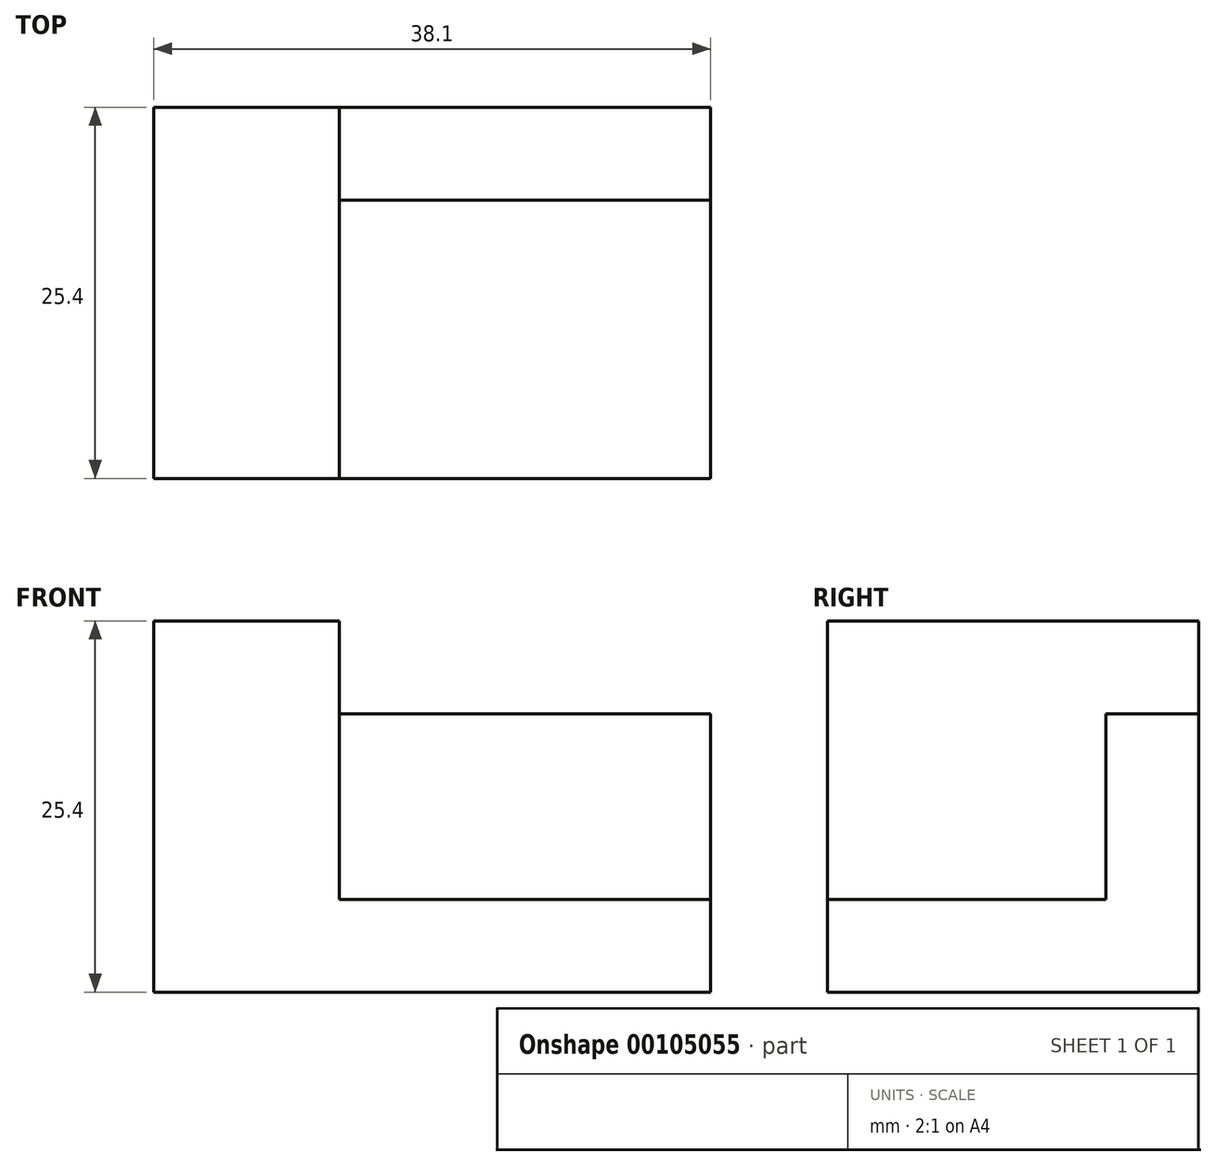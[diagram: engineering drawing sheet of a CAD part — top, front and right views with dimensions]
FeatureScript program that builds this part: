
annotation { "Feature Type Name" : "Feature", "Feature Type Description" : "" }
export const myFeature = defineFeature(function(context is Context, id is Id, definition is map)
    precondition{}
    {
        {
            var Q0;
            Q0=qCreatedBy(makeId("Right.planeOp"),FACE);
            var sketch = newSketch(context, id + "F0", { "sketchPlane" : qUnion([Q0])});
            skLineSegment(sketch, "E0.bottom", {"start": v(0, 0) * mm, "end": v(25.4, 0) * mm});
            skLineSegment(sketch, "E0.top", {"start": v(0, -25.4) * mm, "end": v(25.4, -25.4) * mm});
            skLineSegment(sketch, "E0.left", {"start": v(0, 0) * mm, "end": v(0, -25.4) * mm});
            skLineSegment(sketch, "E0.right", {"start": v(25.4, 0) * mm, "end": v(25.4, -25.4) * mm});
            skLineSegment(sketch, "E1.bottom", {"start": v(25.4, -6.35) * mm, "end": v(19.05, -6.35) * mm});
            skLineSegment(sketch, "E1.top", {"start": v(25.4, -25.4) * mm, "end": v(19.05, -25.4) * mm});
            skLineSegment(sketch, "E1.left", {"start": v(25.4, -6.35) * mm, "end": v(25.4, -25.4) * mm});
            skLineSegment(sketch, "E1.right", {"start": v(19.05, -6.35) * mm, "end": v(19.05, -19.05) * mm});
            skLineSegment(sketch, "E2.bottom", {"start": v(19.05, -19.05) * mm, "end": v(0, -19.05) * mm});
            skLineSegment(sketch, "E2.top", {"start": v(19.05, -25.4) * mm, "end": v(0, -25.4) * mm});
            skLineSegment(sketch, "E2.left", {"start": v(25.4, -19.05) * mm, "end": v(25.4, -25.4) * mm});
            skLineSegment(sketch, "E2.right", {"start": v(0, -19.05) * mm, "end": v(0, -25.4) * mm});
            skSolve(sketch);
        }
        {
            var Q0;
            Q0=makeQuery(id+"F0.imprint","IMPRINT",FACE,{"disambiguationData":[TD([[makeQuery(id+"F0.imprint","IMPRINT",EDGE,{"derivedFrom":sQuery(id+"F0.wireOp",EDGE,"E1.bottom")}),1.0]])]});
            extrude(context, id + "F1", {"entities" : qUnion([Q0]), "depth" : 38.1 * mm});
        }
        {
            var Q0;
            Q0=makeQuery(id+"F0.imprint","IMPRINT",FACE,{"disambiguationData":[TD([[makeQuery(id+"F0.imprint","IMPRINT",EDGE,{"derivedFrom":sQuery(id+"F0.wireOp",EDGE,"E0.bottom")}),-1.0]])]});
            extrude(context, id + "F2", {"entities" : qUnion([Q0]), "operationType" : NewBodyOperationType.ADD, "depth" : 12.7 * mm});
        }
    });
